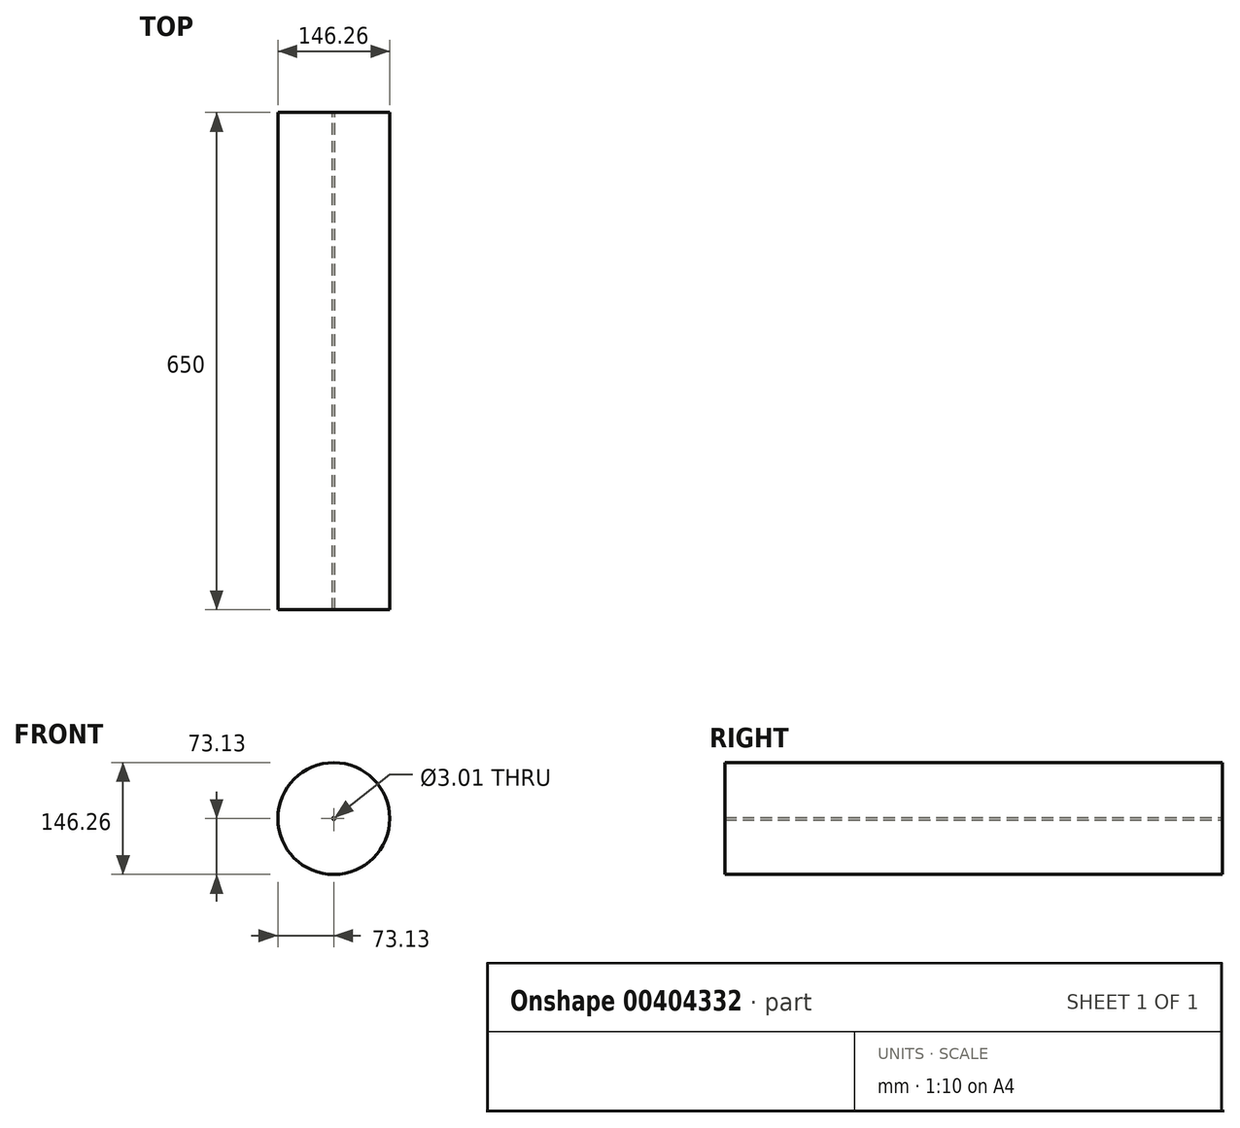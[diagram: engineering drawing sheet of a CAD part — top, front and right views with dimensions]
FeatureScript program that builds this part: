
annotation { "Feature Type Name" : "Feature", "Feature Type Description" : "" }
export const myFeature = defineFeature(function(context is Context, id is Id, definition is map)
    precondition{}
    {
        {
            var Q0;
            Q0=qCreatedBy(makeId("Front.planeOp"),FACE);
            var sketch = newSketch(context, id + "F0", { "sketchPlane" : qUnion([Q0])});
            skCircle(sketch, "E0", {"center": v(0, 0) * mm, "radius": 63.67 * mm});
            skSolve(sketch);
        }
        {
            var Q0;
            Q0=sQuery(id+"F0.wireOp",EDGE,"E0");
            extrude(context, id + "F1", {"bodyType" : ToolBodyType.SURFACE, "surfaceEntities" : qUnion([Q0]), "depth" : 152.4 * mm});
        }
        {
            var Q0;
            Q0=makeQuery(id+"F1.opExtrude","SWEPT_BODY",BODY,{"disambiguationData":[OSD([sQuery(id+"F0.wireOp",EDGE,"E0")])]});
            deleteBodies(context, id + "F2", {"entities" : qUnion([Q0])});
        }
        {
            var Q0;
            Q0=qCreatedBy(makeId("Front.planeOp"),FACE);
            var sketch = newSketch(context, id + "F3", { "sketchPlane" : qUnion([Q0])});
            skCircle(sketch, "E1", {"center": v(0, 0) * mm, "radius": 73.13 * mm});
            skCircle(sketch, "E2", {"center": v(0, 0) * mm, "radius": 1.5 * mm});
            skSolve(sketch);
        }
        {
            var Q0;
            Q0=makeQuery(id+"F3.imprint","IMPRINT",FACE,{"disambiguationData":[TD([[makeQuery(id+"F3.imprint","IMPRINT",EDGE,{"derivedFrom":sQuery(id+"F3.wireOp",EDGE,"E1")}),1.0]])]});
            extrude(context, id + "F4", {"entities" : qUnion([Q0]), "depth" : 650 * mm});
        }
    });
